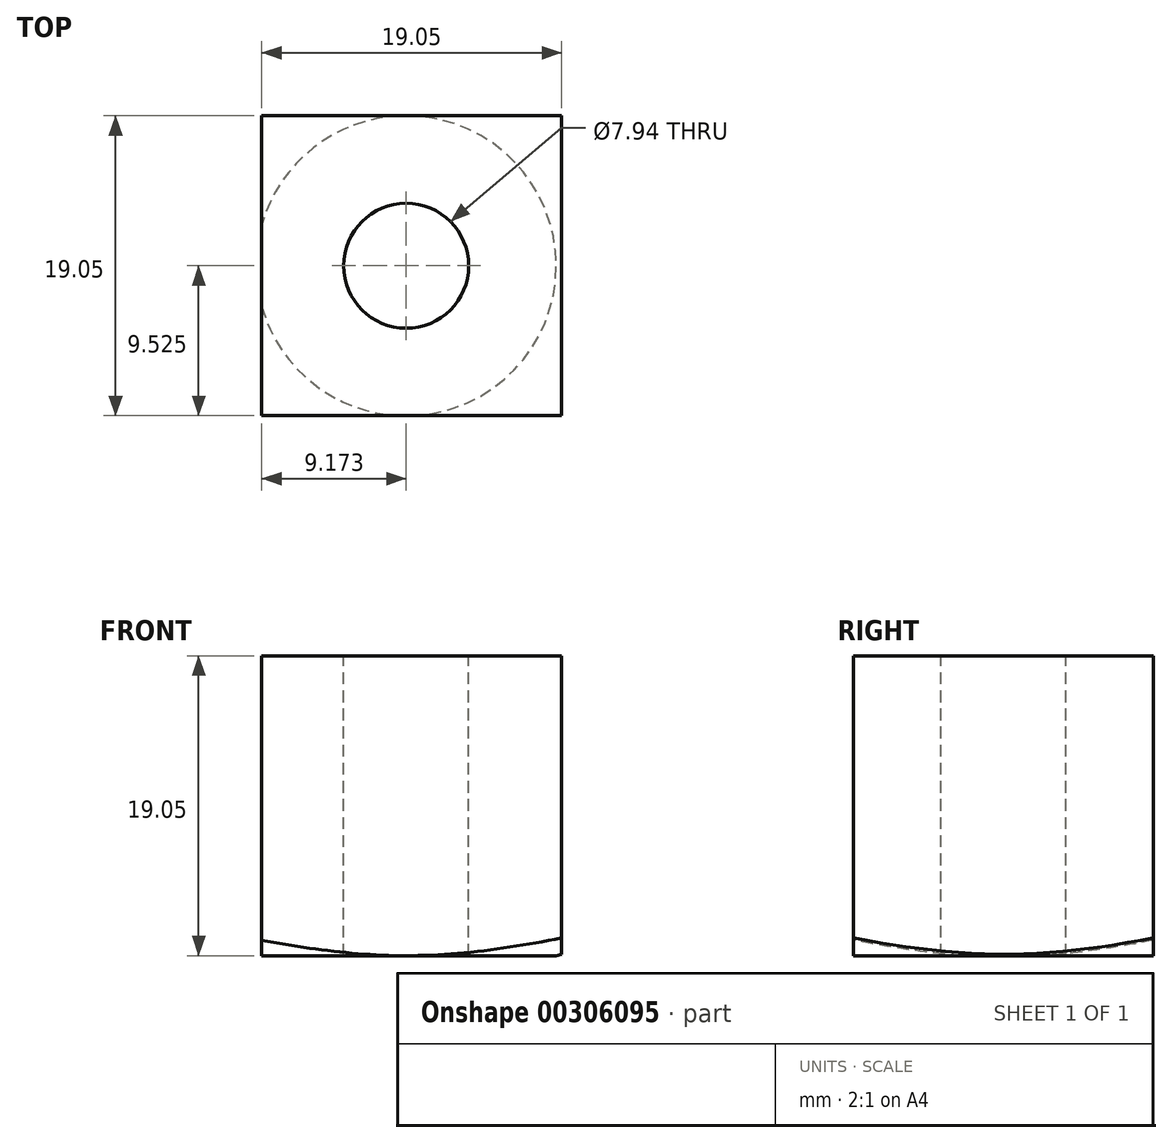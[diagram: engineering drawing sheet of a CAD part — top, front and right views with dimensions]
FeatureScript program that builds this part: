
annotation { "Feature Type Name" : "Feature", "Feature Type Description" : "" }
export const myFeature = defineFeature(function(context is Context, id is Id, definition is map)
    precondition{}
    {
        {
            var Q0;
            Q0=qCreatedBy(makeId("Top.planeOp"),FACE);
            var sketch = newSketch(context, id + "F0", { "sketchPlane" : qUnion([Q0])});
            skLineSegment(sketch, "E0.bottom", {"start": v(0, 0) * mm, "end": v(19.05, 0) * mm});
            skLineSegment(sketch, "E0.top", {"start": v(0, -19.05) * mm, "end": v(19.05, -19.05) * mm});
            skLineSegment(sketch, "E0.left", {"start": v(0, 0) * mm, "end": v(0, -19.05) * mm});
            skLineSegment(sketch, "E0.right", {"start": v(19.05, 0) * mm, "end": v(19.05, -19.05) * mm});
            skSolve(sketch);
        }
        {
            var Q0;
            Q0 = qSketchRegion(id + "F0", true);
            extrude(context, id + "F1", {"entities" : qUnion([Q0]), "depth" : 19.05 * mm});
        }
        {
            var Q0;
            Q0=makeQuery(id+"F1.opExtrude","CAP_FACE",FACE,{"disambiguationData":[OSD([sQuery(id+"F0.wireOp",EDGE,"E0.bottom"),sQuery(id+"F0.wireOp",EDGE,"E0.top"),sQuery(id+"F0.wireOp",EDGE,"E0.left"),sQuery(id+"F0.wireOp",EDGE,"E0.right")])],"isStart":false});
            var sketch = newSketch(context, id + "F2", { "sketchPlane" : qUnion([Q0])});
            skCircle(sketch, "E1", {"center": v(9.17, -9.53) * mm, "radius": 9.53 * mm});
            skCircle(sketch, "E2", {"center": v(9.17, -9.53) * mm, "radius": 3.97 * mm});
            skSolve(sketch);
        }
        {
            var Q0;
            Q0=makeQuery(id+"F2.imprint","IMPRINT",FACE,{"disambiguationData":[TD([[makeQuery(id+"F2.imprint","IMPRINT",EDGE,{"derivedFrom":sQuery(id+"F2.wireOp",EDGE,"E2")}),1.0]])]});
            extrude(context, id + "F3", {"entities" : qUnion([Q0]), "operationType" : NewBodyOperationType.REMOVE, "oppositeDirection" : true, "depth" : 25.4 * mm});
        }
        {
            var Q0;
            Q0=makeQuery(id+"F1.opExtrude","SWEPT_FACE",FACE,{"disambiguationData":[OSD([sQuery(id+"F0.wireOp",EDGE,"E0.right")])]});
            var Q1;
            Q1=makeQuery(id+"F1.opExtrude","SWEPT_FACE",FACE,{"disambiguationData":[OSD([sQuery(id+"F0.wireOp",EDGE,"E0.left")])]});
            cPlane(context, id + "F4", {"entities" : qUnion([Q0, Q1]), "cplaneType" : CPlaneType.MID_PLANE, "offset" : 25.4 * mm, "width" : 152.4 * mm, "height" : 152.4 * mm});
        }
        {
            var Q0;
            Q0=qCreatedBy(id+"F4.planeOp",FACE);
            var sketch = newSketch(context, id + "F5", { "sketchPlane" : qUnion([Q0])});
            skLineSegment(sketch, "E3.0.0", {"start": v(-19.05, 0) * mm, "end": v(0, 0) * mm});
            skLineSegment(sketch, "E3.0.1", {"start": v(0, 0) * mm, "end": v(0, 19.05) * mm});
            skLineSegment(sketch, "E3.0.2", {"start": v(0, 19.05) * mm, "end": v(-19.05, 19.05) * mm});
            skLineSegment(sketch, "E3.0.3", {"start": v(-19.05, 19.05) * mm, "end": v(-19.05, 0) * mm});
            skLineSegment(sketch, "E4", {"start": v(-19.05, 0) * mm, "end": v(-29.03, 0) * mm});
            skLineSegment(sketch, "E5", {"start": v(-29.03, 0) * mm, "end": v(-29.03, 2.67) * mm});
            skLineSegment(sketch, "E6", {"start": v(-29.03, 2.67) * mm, "end": v(-19.05, 0) * mm});
            skSolve(sketch);
        }
        {
            var Q0;
            Q0=makeQuery(id+"F5.imprint","IMPRINT",FACE,{"disambiguationData":[TD([[makeQuery(id+"F5.imprint","IMPRINT",EDGE,{"derivedFrom":sQuery(id+"F5.wireOp",EDGE,"E4")}),-1.0]])]});
            var Q1;
            Q1=makeQuery(id+"F3.boolean.opBoolean","COPY",FACE,{"derivedFrom":makeQuery(id+"F3.opExtrude","SWEPT_FACE",FACE,{"disambiguationData":[OSD([sQuery(id+"F2.wireOp",EDGE,"E2")])]})});
            revolve(context, id + "F6", {"operationType" : NewBodyOperationType.REMOVE, "entities" : qUnion([Q0]), "axis" : qUnion([Q1]), "revolveType" : RevolveType.FULL, "oppositeDirection" : true});
        }
    });
